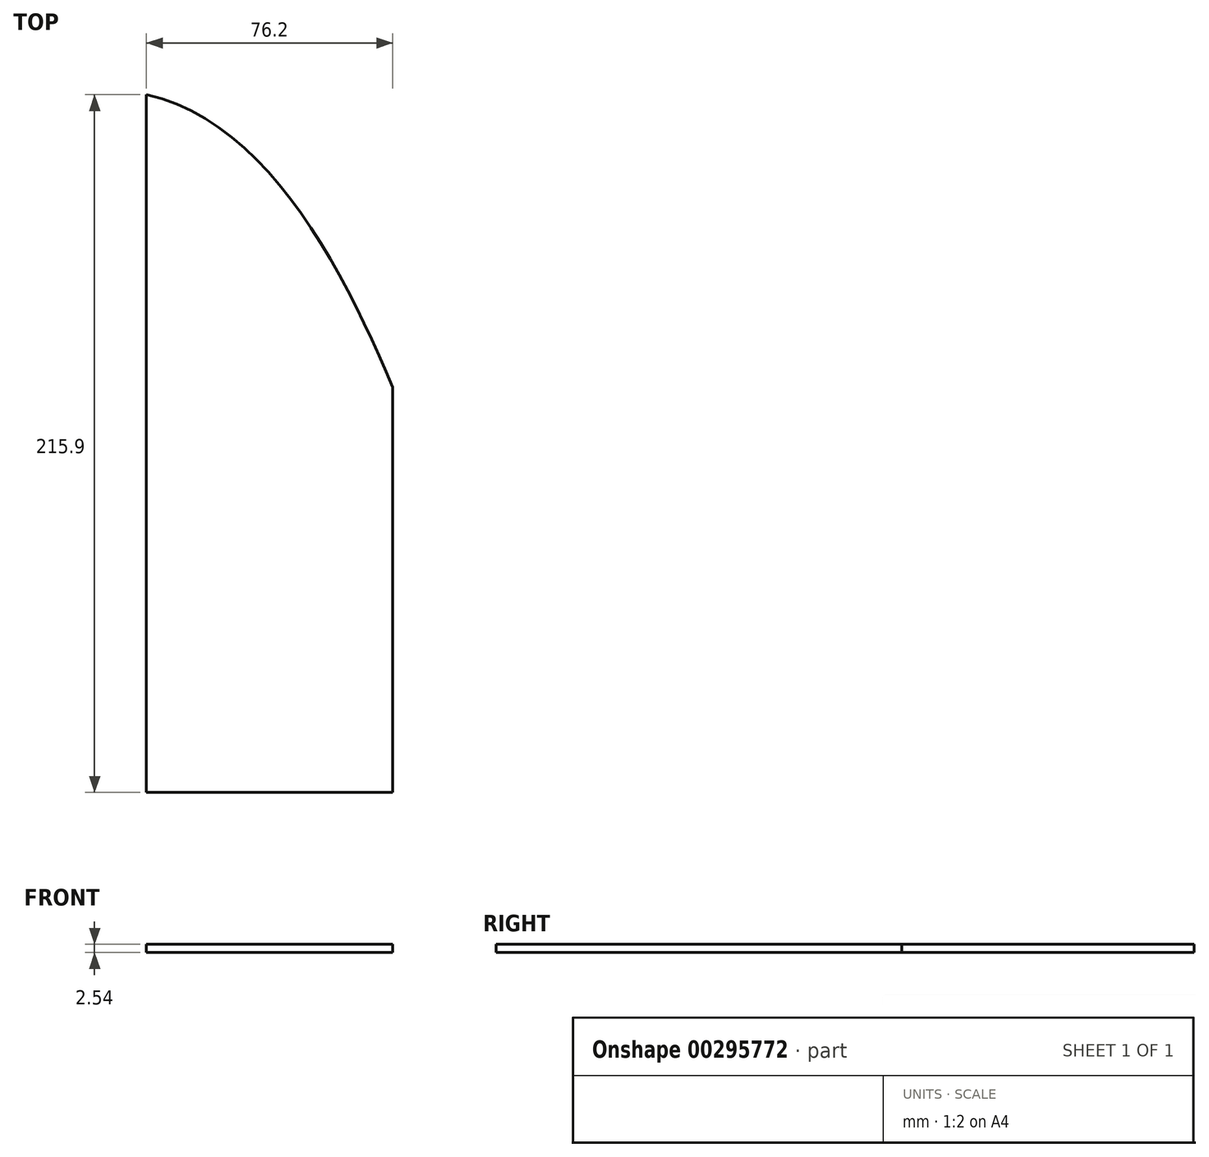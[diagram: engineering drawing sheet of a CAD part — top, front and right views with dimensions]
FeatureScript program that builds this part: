
annotation { "Feature Type Name" : "Feature", "Feature Type Description" : "" }
export const myFeature = defineFeature(function(context is Context, id is Id, definition is map)
    precondition{}
    {
        {
            var Q0;
            Q0=qCreatedBy(makeId("Top.planeOp"),FACE);
            var sketch = newSketch(context, id + "F0", { "sketchPlane" : qUnion([Q0])});
            skLineSegment(sketch, "E0.bottom", {"start": v(0, 0) * mm, "end": v(76.2, 0) * mm});
            skLineSegment(sketch, "E0.left", {"start": v(0, 0) * mm, "end": v(0, 215.9) * mm});
            skFitSpline(sketch, "E1", {"points": [v(0, 215.9) * mm, v(76.2, 125.4) * mm], "startDerivative": vector(111.38, -24.22) * mm, "endDerivative": vector(46.79, -111) * mm});
            skLineSegment(sketch, "E2", {"start": v(76.2, 125.4) * mm, "end": v(76.2, 0) * mm});
            skSolve(sketch);
        }
        {
            var Q0;
            Q0 = qSketchRegion(id + "F0", true);
            extrude(context, id + "F1", {"entities" : qUnion([Q0]), "depth" : 2.54 * mm});
        }
    });
